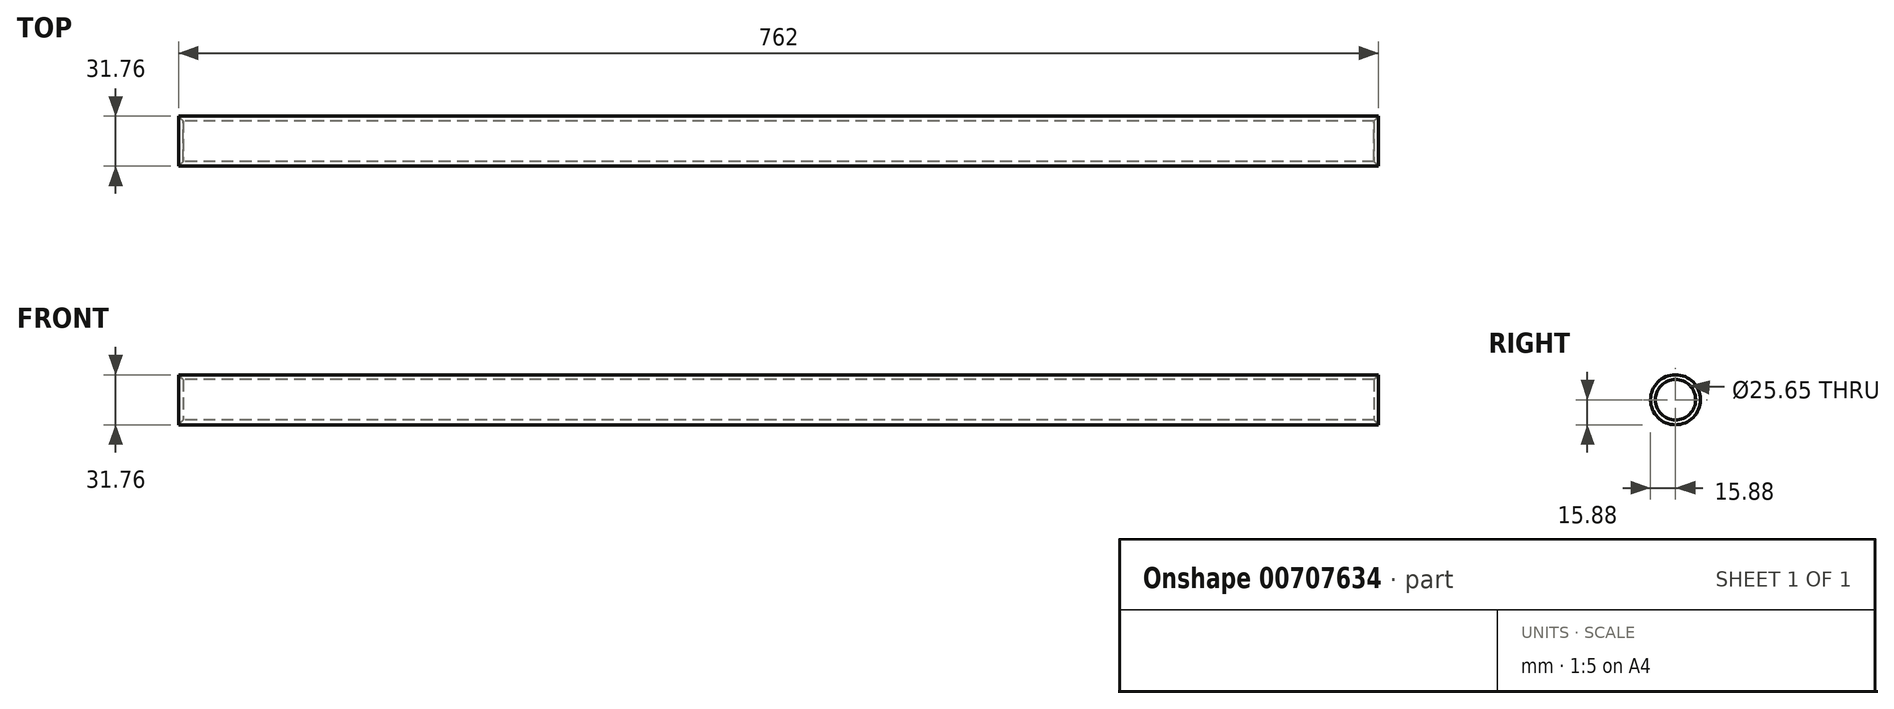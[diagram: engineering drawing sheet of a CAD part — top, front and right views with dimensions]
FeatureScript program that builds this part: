
annotation { "Feature Type Name" : "Feature", "Feature Type Description" : "" }
export const myFeature = defineFeature(function(context is Context, id is Id, definition is map)
    precondition{}
    {
        {
            var Q0;
            Q0=qCreatedBy(makeId("Front.planeOp"),FACE);
            var sketch = newSketch(context, id + "F0", { "sketchPlane" : qUnion([Q0])});
            skLineSegment(sketch, "E0", {"start": v(0, 0) * mm, "end": v(762, 0) * mm, "construction": true});
            skLineSegment(sketch, "E1", {"start": v(0, 15.88) * mm, "end": v(762, 15.88) * mm});
            skLineSegment(sketch, "E2", {"start": v(0, 15.88) * mm, "end": v(2.74, 12.83) * mm});
            skLineSegment(sketch, "E3", {"start": v(762, 15.88) * mm, "end": v(759.26, 12.83) * mm});
            skLineSegment(sketch, "E4", {"start": v(759.26, 12.83) * mm, "end": v(2.74, 12.83) * mm});
            skSolve(sketch);
        }
        {
            var Q0;
            Q0=qSketchRegion(id+"F0",true);
            var Q1;
            Q1=sQuery(id+"F0.wireOp",EDGE,"E0");
            revolve(context, id + "F1", {"entities" : qUnion([Q0]), "axis" : qUnion([Q1]), "revolveType" : RevolveType.FULL});
        }
    });
